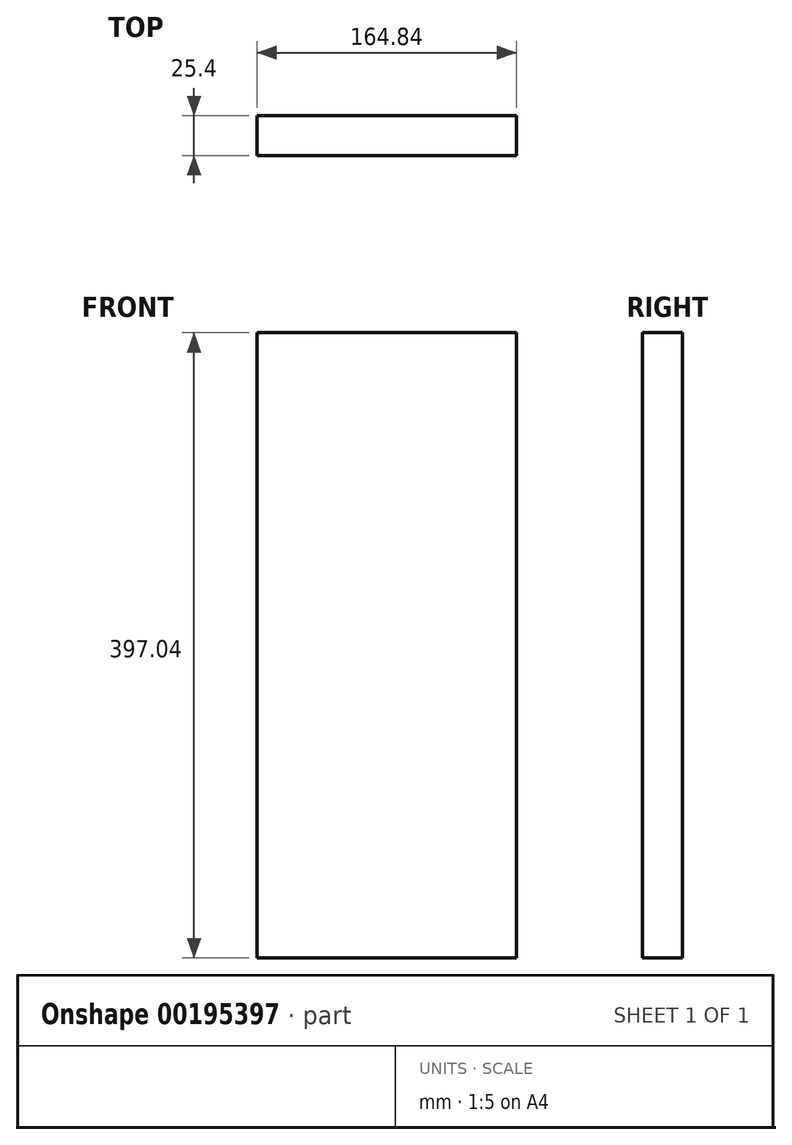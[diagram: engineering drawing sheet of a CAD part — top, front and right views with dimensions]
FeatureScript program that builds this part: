
annotation { "Feature Type Name" : "Feature", "Feature Type Description" : "" }
export const myFeature = defineFeature(function(context is Context, id is Id, definition is map)
    precondition{}
    {
        {
            var Q0;
            Q0=qCreatedBy(makeId("Front.planeOp"),FACE);
            var sketch = newSketch(context, id + "F0", { "sketchPlane" : qUnion([Q0])});
            skLineSegment(sketch, "E0.bottom", {"start": v(82.42, -198.52) * mm, "end": v(-82.42, -198.52) * mm});
            skLineSegment(sketch, "E0.top", {"start": v(82.42, 198.52) * mm, "end": v(-82.42, 198.52) * mm});
            skLineSegment(sketch, "E0.left", {"start": v(82.42, -198.52) * mm, "end": v(82.42, 198.52) * mm});
            skLineSegment(sketch, "E0.right", {"start": v(-82.42, -198.52) * mm, "end": v(-82.42, 198.52) * mm});
            skPoint(sketch, "E0.middle", {"position": v(0, 0) * mm});
            skSolve(sketch);
        }
        {
            var Q0;
            Q0 = qSketchRegion(id + "F0", true);
            extrude(context, id + "F1", {"entities" : qUnion([Q0]), "depth" : 25.4 * mm});
        }
    });
